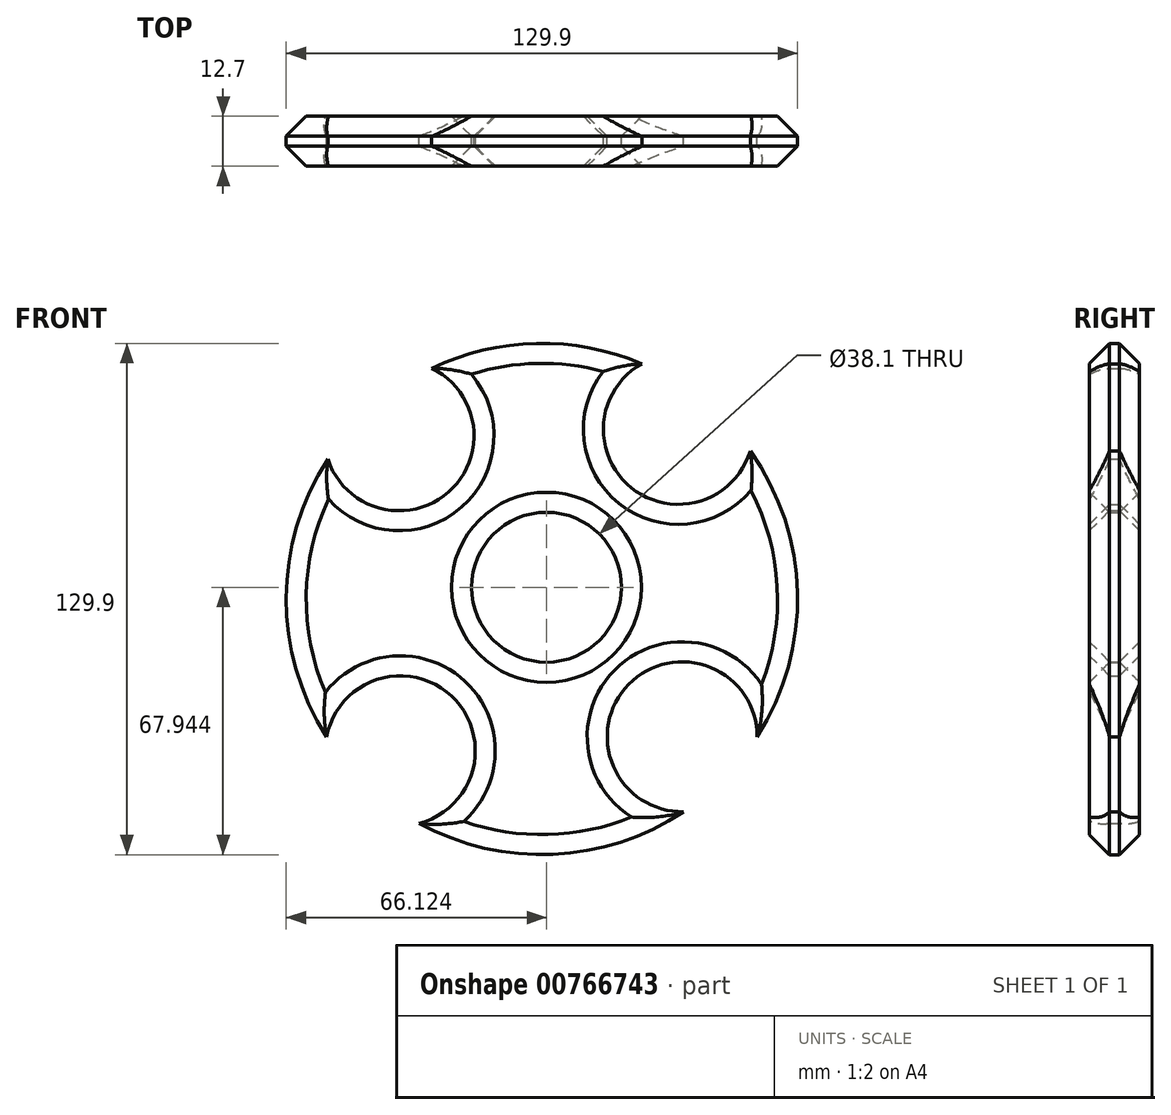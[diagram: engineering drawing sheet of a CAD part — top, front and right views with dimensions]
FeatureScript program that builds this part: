
annotation { "Feature Type Name" : "Feature", "Feature Type Description" : "" }
export const myFeature = defineFeature(function(context is Context, id is Id, definition is map)
    precondition{}
    {
        {
            var Q0;
            Q0=qCreatedBy(makeId("Front.planeOp"),FACE);
            var sketch = newSketch(context, id + "F0", { "sketchPlane" : qUnion([Q0])});
            skCircle(sketch, "E0", {"center": v(-152.92, -21.02) * mm, "radius": 64.95 * mm});
            skSolve(sketch);
        }
        {
            var Q0;
            Q0 = qSketchRegion(id + "F0", true);
            extrude(context, id + "F1", {"entities" : qUnion([Q0]), "depth" : 12.7 * mm, "offsetDistance" : 25.4 * mm});
        }
        {
            var Q0;
            Q0=qCreatedBy(makeId("Front.planeOp"),FACE);
            var sketch = newSketch(context, id + "F2", { "sketchPlane" : qUnion([Q0])});
            skPoint(sketch, "E1", {"position": v(-151.75, -18.03) * mm});
            skPoint(sketch, "E2", {"position": v(-118.24, 22.08) * mm});
            skPoint(sketch, "E3", {"position": v(-189.21, 20.46) * mm});
            skPoint(sketch, "E4", {"position": v(-188.89, -59.58) * mm});
            skPoint(sketch, "E5", {"position": v(-117.27, -56.02) * mm});
            skSolve(sketch);
        }
        {
            var Q0;
            Q0=sQuery(id+"F2.wireOp",VERTEX,"E1");
            var Q1;
            Q1=sQuery(id+"F2.wireOp",VERTEX,"E2");
            var Q2;
            Q2=sQuery(id+"F2.wireOp",VERTEX,"E3");
            var Q3;
            Q3=sQuery(id+"F2.wireOp",VERTEX,"E4");
            var Q4;
            Q4=sQuery(id+"F2.wireOp",VERTEX,"E5");
            var Q5;
            Q5=makeQuery(id+"F1.opExtrude","SWEPT_BODY",BODY,{"disambiguationData":[OSD([sQuery(id+"F0.wireOp",EDGE,"E0")])]});
            hole(context, id + "F3", {"style" : HoleStyle.SIMPLE, "endStyle" : HoleEndStyle.THROUGH, "oppositeDirection" : true, "holeDiameter" : 38.1 * mm, "majorDiameter" : 6.35 * mm, "isTappedThrough" : true, "tappedDepth" : 12.7 * mm, "tapClearance" : 3, "locations" : qUnion([Q0, Q1, Q2, Q3, Q4]), "scope" : qUnion([Q5])});
        }
        {
            var Q0;
            Q0=makeQuery(id+"F1.opExtrude","CAP_FACE",FACE,{"disambiguationData":[OSD([sQuery(id+"F0.wireOp",EDGE,"E0")])],"isStart":false});
            var Q1;
            Q1=makeQuery(id+"F3.hole-4.boolean.opBoolean","COPY",EDGE,{"derivedFrom":makeQuery(id+"F3.hole-4.opRevolve","SWEPT_EDGE",EDGE,{"disambiguationData":[OSD([sQuery(id+"F3.hole-4.sketch.wireOp",EDGE,"core_line_2"),sQuery(id+"F3.hole-4.sketch.wireOp",EDGE,"core_line_3")])]})});
            var Q2;
            Q2=makeQuery(id+"F3.hole-3.boolean.opBoolean","COPY",EDGE,{"derivedFrom":makeQuery(id+"F3.hole-3.opRevolve","SWEPT_EDGE",EDGE,{"disambiguationData":[OSD([sQuery(id+"F3.hole-3.sketch.wireOp",EDGE,"core_line_2"),sQuery(id+"F3.hole-3.sketch.wireOp",EDGE,"core_line_3")])]})});
            var Q3;
            Q3=makeQuery(id+"F3.hole-2.boolean.opBoolean","COPY",EDGE,{"derivedFrom":makeQuery(id+"F3.hole-2.opRevolve","SWEPT_EDGE",EDGE,{"disambiguationData":[OSD([sQuery(id+"F3.hole-2.sketch.wireOp",EDGE,"core_line_2"),sQuery(id+"F3.hole-2.sketch.wireOp",EDGE,"core_line_3")])]})});
            var Q4;
            Q4=makeQuery(id+"F3.hole-1.boolean.opBoolean","COPY",EDGE,{"derivedFrom":makeQuery(id+"F3.hole-1.opRevolve","SWEPT_EDGE",EDGE,{"disambiguationData":[OSD([sQuery(id+"F3.hole-1.sketch.wireOp",EDGE,"core_line_2"),sQuery(id+"F3.hole-1.sketch.wireOp",EDGE,"core_line_3")])]})});
            var Q5;
            Q5=makeQuery(id+"F3.hole-0.boolean.opBoolean","COPY",EDGE,{"derivedFrom":makeQuery(id+"F3.hole-0.opRevolve","SWEPT_EDGE",EDGE,{"disambiguationData":[OSD([sQuery(id+"F3.hole-0.sketch.wireOp",EDGE,"core_line_2"),sQuery(id+"F3.hole-0.sketch.wireOp",EDGE,"core_line_3")])]})});
            var Q6;
            {var subQ0=sQuery(id+"F0.wireOp",EDGE,"E0");var subQ2=makeQuery(id+"F3.hole-1.boolean.opBoolean","COPY",FACE,{"derivedFrom":makeQuery(id+"F3.hole-1.opRevolve","SWEPT_FACE",FACE,{"disambiguationData":[OSD([sQuery(id+"F3.hole-1.sketch.wireOp",EDGE,"core_line_2")])]})});Q6=makeQuery(id+"F3.hole-4.boolean.opBoolean","SPLIT",EDGE,{"disambiguationData":[TD([subQ2])],"derivedFrom":makeQuery(id+"F3.hole-3.boolean.opBoolean","SPLIT",EDGE,{"disambiguationData":[TD([subQ2])],"derivedFrom":makeQuery(id+"F3.hole-2.boolean.opBoolean","SPLIT",EDGE,{"disambiguationData":[OD(1.0)],"derivedFrom":makeQuery(id+"F1.opExtrude","CAP_EDGE",EDGE,{"disambiguationData":[OSD([subQ0])],"isStart":true})})})});}
            var Q7;
            {var subQ0=sQuery(id+"F0.wireOp",EDGE,"E0");Q7=makeQuery(id+"F3.hole-3.boolean.opBoolean","SPLIT",EDGE,{"disambiguationData":[TD([makeQuery(id+"F3.hole-2.boolean.opBoolean","COPY",FACE,{"derivedFrom":makeQuery(id+"F3.hole-2.opRevolve","SWEPT_FACE",FACE,{"disambiguationData":[OSD([sQuery(id+"F3.hole-2.sketch.wireOp",EDGE,"core_line_2")])]})})])],"derivedFrom":makeQuery(id+"F3.hole-2.boolean.opBoolean","SPLIT",EDGE,{"disambiguationData":[OD(1.0)],"derivedFrom":makeQuery(id+"F1.opExtrude","CAP_EDGE",EDGE,{"disambiguationData":[OSD([subQ0])],"isStart":true})})});}
            var Q8;
            Q8=makeQuery(id+"F1.opExtrude","CAP_FACE",FACE,{"disambiguationData":[OSD([sQuery(id+"F0.wireOp",EDGE,"E0")])],"isStart":true});
            chamfer(context, id + "F4", {"entities" : qUnion([Q0, Q1, Q2, Q3, Q4, Q5, Q6, Q7, Q8]), "width" : 5.08 * mm, "tangentPropagation" : true});
        }
    });
